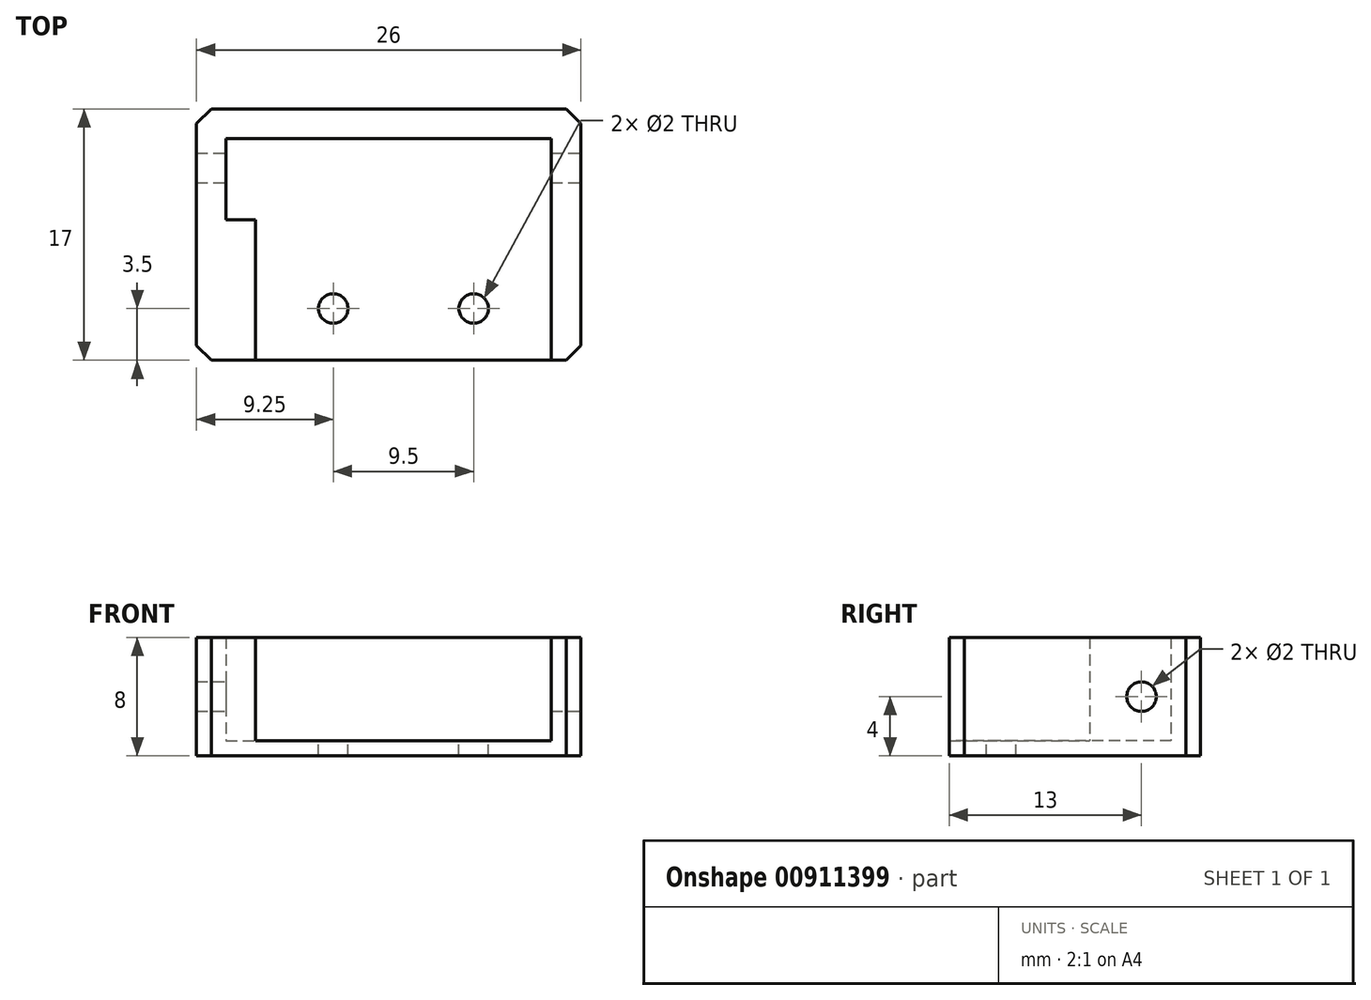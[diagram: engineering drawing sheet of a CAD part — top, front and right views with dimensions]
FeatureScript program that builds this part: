
annotation { "Feature Type Name" : "Feature", "Feature Type Description" : "" }
export const myFeature = defineFeature(function(context is Context, id is Id, definition is map)
    precondition{}
    {
        {
            var Q0;
            Q0=qCreatedBy(makeId("Top.planeOp"),FACE);
            var sketch = newSketch(context, id + "F0", { "sketchPlane" : qUnion([Q0])});
            skLineSegment(sketch, "E0.top", {"start": v(-10, 0) * mm, "end": v(10, 0) * mm});
            skLineSegment(sketch, "E0.left", {"start": v(-10, 9.5) * mm, "end": v(-10, 0) * mm});
            skLineSegment(sketch, "E0.right", {"start": v(10, 9.5) * mm, "end": v(10, 0) * mm});
            skLineSegment(sketch, "E1.bottom", {"start": v(-10, 9.5) * mm, "end": v(-12, 9.5) * mm});
            skLineSegment(sketch, "E1.top", {"start": v(10, 15) * mm, "end": v(-12, 15) * mm});
            skLineSegment(sketch, "E1.left", {"start": v(10, 9.5) * mm, "end": v(10, 15) * mm});
            skLineSegment(sketch, "E1.right", {"start": v(-12, 9.5) * mm, "end": v(-12, 15) * mm});
            skLineSegment(sketch, "E2", {"start": v(-14, 0) * mm, "end": v(-14, 17) * mm});
            skLineSegment(sketch, "E3", {"start": v(-14, 17) * mm, "end": v(12, 17) * mm});
            skLineSegment(sketch, "E4", {"start": v(12, 17) * mm, "end": v(12, 0) * mm});
            skLineSegment(sketch, "E5", {"start": v(12, 0) * mm, "end": v(10, 0) * mm});
            skLineSegment(sketch, "E6", {"start": v(-10, 0) * mm, "end": v(-14, 0) * mm});
            skCircle(sketch, "E7", {"center": v(4.75, 3.5) * mm, "radius": 1 * mm});
            skCircle(sketch, "E8", {"center": v(-4.75, 3.5) * mm, "radius": 1 * mm});
            skSolve(sketch);
        }
        {
            var Q0;
            Q0=makeQuery(id+"F0.imprint","IMPRINT",FACE,{"disambiguationData":[TD([[makeQuery(id+"F0.imprint","IMPRINT",EDGE,{"derivedFrom":sQuery(id+"F0.wireOp",EDGE,"E0.top")}),1.0]])]});
            var Q1;
            Q1=makeQuery(id+"F0.imprint","IMPRINT",FACE,{"disambiguationData":[TD([[makeQuery(id+"F0.imprint","IMPRINT",EDGE,{"derivedFrom":sQuery(id+"F0.wireOp",EDGE,"E8")}),1.0]])]});
            var Q2;
            Q2=makeQuery(id+"F0.imprint","IMPRINT",FACE,{"disambiguationData":[TD([[makeQuery(id+"F0.imprint","IMPRINT",EDGE,{"derivedFrom":sQuery(id+"F0.wireOp",EDGE,"E7")}),1.0]])]});
            var Q3;
            Q3=makeQuery(id+"F0.imprint","IMPRINT",FACE,{"disambiguationData":[TD([[makeQuery(id+"F0.imprint","IMPRINT",EDGE,{"derivedFrom":sQuery(id+"F0.wireOp",EDGE,"E0.left")}),-1.0]])]});
            extrude(context, id + "F1", {"entities" : qUnion([Q0, Q1, Q2, Q3]), "depth" : 1 * mm, "offsetDistance" : 25 * mm});
        }
        {
            var Q0;
            Q0=makeQuery(id+"F0.imprint","IMPRINT",FACE,{"disambiguationData":[TD([[makeQuery(id+"F0.imprint","IMPRINT",EDGE,{"derivedFrom":sQuery(id+"F0.wireOp",EDGE,"E0.left")}),-1.0]])]});
            var Q1;
            Q1=makeQuery(id+"F0.imprint","IMPRINT",FACE,{"disambiguationData":[TD([[makeQuery(id+"F0.imprint","IMPRINT",EDGE,{"derivedFrom":sQuery(id+"F0.wireOp",EDGE,"E8")}),1.0]])]});
            var Q2;
            Q2=makeQuery(id+"F0.imprint","IMPRINT",FACE,{"disambiguationData":[TD([[makeQuery(id+"F0.imprint","IMPRINT",EDGE,{"derivedFrom":sQuery(id+"F0.wireOp",EDGE,"E7")}),1.0]])]});
            extrude(context, id + "F2", {"entities" : qUnion([Q0, Q1, Q2]), "operationType" : NewBodyOperationType.ADD, "depth" : 8 * mm, "offsetDistance" : 25 * mm});
        }
        {
            var Q0;
            Q0=makeQuery(id+"F2.opExtrude","CAP_FACE",FACE,{"disambiguationData":[OSD([sQuery(id+"F0.wireOp",EDGE,"E8")])],"isStart":false});
            var Q1;
            Q1=makeQuery(id+"F2.opExtrude","CAP_FACE",FACE,{"disambiguationData":[OSD([sQuery(id+"F0.wireOp",EDGE,"E7")])],"isStart":false});
            extrude(context, id + "F3", {"entities" : qUnion([Q0, Q1]), "operationType" : NewBodyOperationType.REMOVE, "oppositeDirection" : true, "depth" : 10 * mm, "offsetDistance" : 25 * mm});
        }
        {
            var Q0;
            {var subQ0=sQuery(id+"F0.wireOp",EDGE,"E4");Q0=makeQuery(id+"F2.boolean.opBoolean","MERGE",FACE,{"derivedFrom":[makeQuery(id+"F1.opExtrude","SWEPT_FACE",FACE,{"disambiguationData":[OSD([subQ0])]}),makeQuery(id+"F2.opExtrude","SWEPT_FACE",FACE,{"disambiguationData":[OSD([subQ0])]})]});}
            var sketch = newSketch(context, id + "F4", { "sketchPlane" : qUnion([Q0])});
            skCircle(sketch, "E9", {"center": v(13, 4) * mm, "radius": 1 * mm});
            skSolve(sketch);
        }
        {
            var Q0;
            Q0=makeQuery(id+"F4.imprint","IMPRINT",FACE,{"disambiguationData":[TD([[makeQuery(id+"F4.imprint","IMPRINT",EDGE,{"derivedFrom":sQuery(id+"F4.wireOp",EDGE,"E9")}),1.0]])]});
            extrude(context, id + "F5", {"entities" : qUnion([Q0]), "operationType" : NewBodyOperationType.REMOVE, "oppositeDirection" : true, "depth" : 30 * mm, "offsetDistance" : 25 * mm});
        }
        {
            var Q0;
            {var subQ0=sQuery(id+"F0.wireOp",EDGE,"E3");var subQ1=sQuery(id+"F0.wireOp",EDGE,"E2");Q0=makeQuery(id+"F2.boolean.opBoolean","MERGE",EDGE,{"derivedFrom":[makeQuery(id+"F1.opExtrude","SWEPT_EDGE",EDGE,{"disambiguationData":[OSD([subQ1,subQ0])]}),makeQuery(id+"F2.opExtrude","SWEPT_EDGE",EDGE,{"disambiguationData":[OSD([subQ1,subQ0])]})]});}
            var Q1;
            {var subQ0=sQuery(id+"F0.wireOp",EDGE,"E4");var subQ1=sQuery(id+"F0.wireOp",EDGE,"E3");Q1=makeQuery(id+"F2.boolean.opBoolean","MERGE",EDGE,{"derivedFrom":[makeQuery(id+"F1.opExtrude","SWEPT_EDGE",EDGE,{"disambiguationData":[OSD([subQ1,subQ0])]}),makeQuery(id+"F2.opExtrude","SWEPT_EDGE",EDGE,{"disambiguationData":[OSD([subQ1,subQ0])]})]});}
            var Q2;
            {var subQ0=sQuery(id+"F0.wireOp",EDGE,"E6");var subQ1=sQuery(id+"F0.wireOp",EDGE,"E2");Q2=makeQuery(id+"F2.boolean.opBoolean","MERGE",EDGE,{"derivedFrom":[makeQuery(id+"F1.opExtrude","SWEPT_EDGE",EDGE,{"disambiguationData":[OSD([subQ1,subQ0])]}),makeQuery(id+"F2.opExtrude","SWEPT_EDGE",EDGE,{"disambiguationData":[OSD([subQ1,subQ0])]})]});}
            var Q3;
            {var subQ0=sQuery(id+"F0.wireOp",EDGE,"E5");var subQ1=sQuery(id+"F0.wireOp",EDGE,"E4");Q3=makeQuery(id+"F2.boolean.opBoolean","MERGE",EDGE,{"derivedFrom":[makeQuery(id+"F1.opExtrude","SWEPT_EDGE",EDGE,{"disambiguationData":[OSD([subQ1,subQ0])]}),makeQuery(id+"F2.opExtrude","SWEPT_EDGE",EDGE,{"disambiguationData":[OSD([subQ1,subQ0])]})]});}
            chamfer(context, id + "F6", {"entities" : qUnion([Q0, Q1, Q2, Q3]), "width" : 1 * mm, "tangentPropagation" : true});
        }
    });
